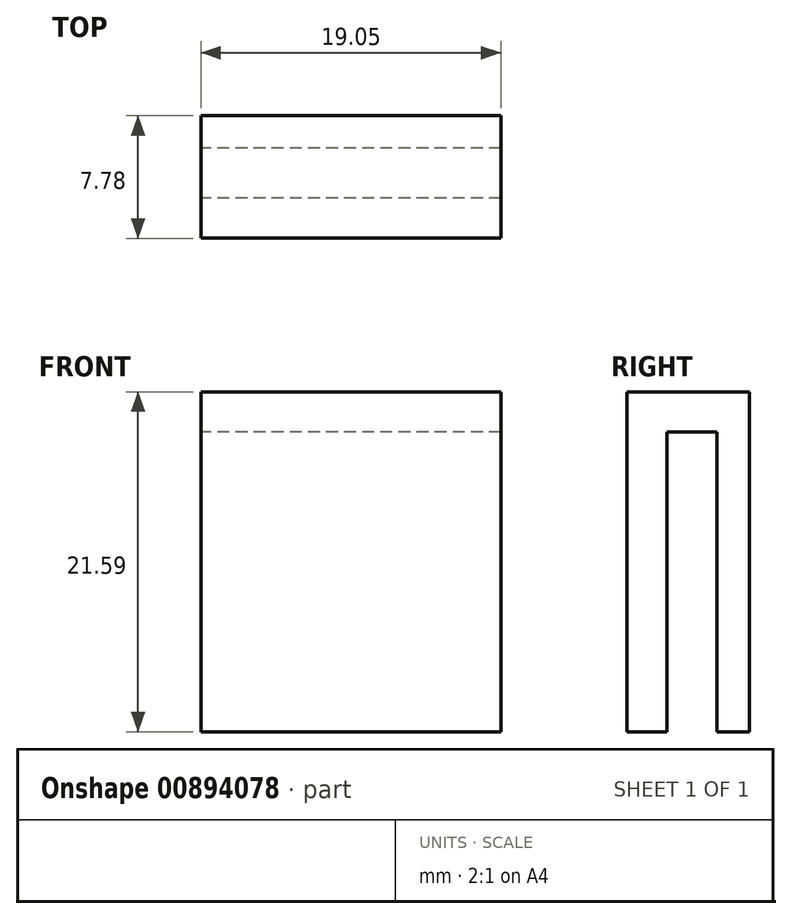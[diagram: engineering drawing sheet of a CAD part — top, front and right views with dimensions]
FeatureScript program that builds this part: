
annotation { "Feature Type Name" : "Feature", "Feature Type Description" : "" }
export const myFeature = defineFeature(function(context is Context, id is Id, definition is map)
    precondition{}
    {
        {
            var Q0;
            Q0=qCreatedBy(makeId("Right.planeOp"),FACE);
            var sketch = newSketch(context, id + "F0", { "sketchPlane" : qUnion([Q0])});
            skLineSegment(sketch, "E0.bottom", {"start": v(-4.13, 21.59) * mm, "end": v(3.65, 21.59) * mm});
            skLineSegment(sketch, "E0.top", {"start": v(-4.13, 0) * mm, "end": v(-1.59, 0) * mm});
            skLineSegment(sketch, "E0.left", {"start": v(-4.13, 21.59) * mm, "end": v(-4.13, 0) * mm});
            skLineSegment(sketch, "E0.right", {"start": v(3.65, 21.59) * mm, "end": v(3.65, 0) * mm});
            skLineSegment(sketch, "E1.top", {"start": v(-1.59, 19.05) * mm, "end": v(1.59, 19.05) * mm});
            skLineSegment(sketch, "E1.left", {"start": v(-1.59, 0) * mm, "end": v(-1.59, 19.05) * mm});
            skLineSegment(sketch, "E1.right", {"start": v(1.59, 0) * mm, "end": v(1.59, 19.05) * mm});
            skPoint(sketch, "E2", {"position": v(0, 19.05) * mm});
            skPoint(sketch, "E3", {"position": v(0, 21.59) * mm});
            skLineSegment(sketch, "E4.trimOffspring", {"start": v(1.59, 0) * mm, "end": v(3.65, 0) * mm});
            skSolve(sketch);
        }
        {
            var Q0;
            Q0 = qSketchRegion(id + "F0", true);
            extrude(context, id + "F1", {"entities" : qUnion([Q0]), "depth" : 19.05 * mm, "offsetDistance" : 25.4 * mm});
        }
    });
